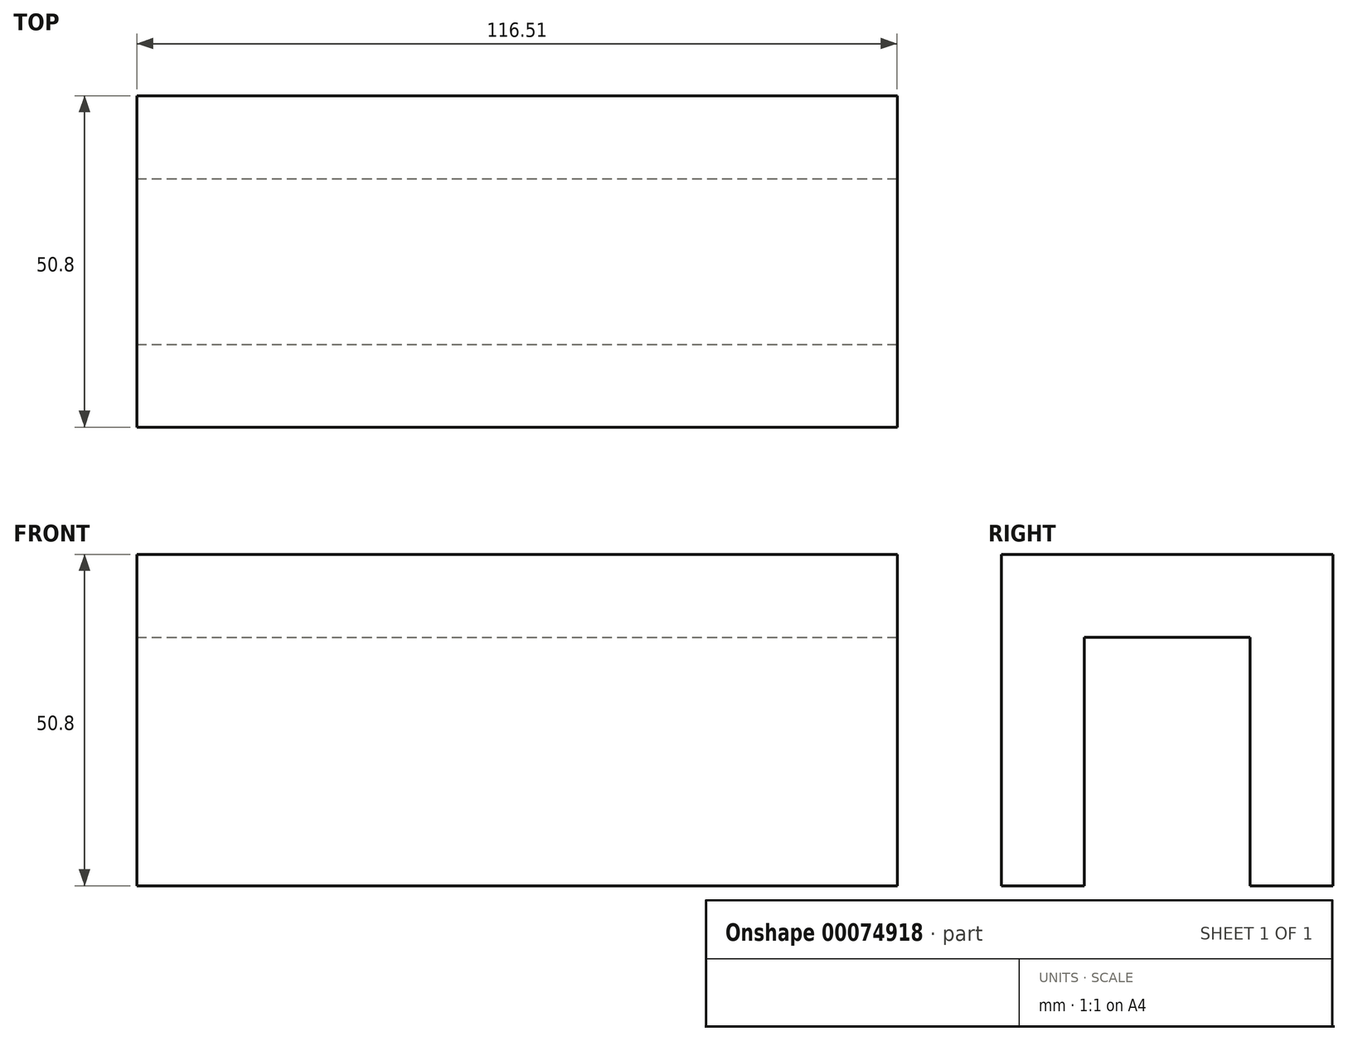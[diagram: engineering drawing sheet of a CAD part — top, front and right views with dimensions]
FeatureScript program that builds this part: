
annotation { "Feature Type Name" : "Feature", "Feature Type Description" : "" }
export const myFeature = defineFeature(function(context is Context, id is Id, definition is map)
    precondition{}
    {
        {
            var Q0;
            Q0=qCreatedBy(makeId("Top.planeOp"),FACE);
            var sketch = newSketch(context, id + "F0", { "sketchPlane" : qUnion([Q0])});
            skLineSegment(sketch, "E0", {"start": v(57.24, 0) * mm, "end": v(57.24, 50.8) * mm});
            skLineSegment(sketch, "E1", {"start": v(57.24, 50.8) * mm, "end": v(-59.27, 50.8) * mm});
            skLineSegment(sketch, "E2", {"start": v(-59.27, 50.8) * mm, "end": v(-59.27, 0) * mm});
            skLineSegment(sketch, "E3", {"start": v(-59.27, 0) * mm, "end": v(57.24, 0) * mm});
            skSolve(sketch);
        }
        {
            var Q0;
            Q0 = qSketchRegion(id + "F0", true);
            extrude(context, id + "F1", {"entities" : qUnion([Q0]), "depth" : 12.7 * mm});
        }
        {
            var Q0;
            Q0=makeQuery(id+"F1.opExtrude","CAP_FACE",FACE,{"disambiguationData":[OSD([sQuery(id+"F0.wireOp",EDGE,"E0"),sQuery(id+"F0.wireOp",EDGE,"E1"),sQuery(id+"F0.wireOp",EDGE,"E2"),sQuery(id+"F0.wireOp",EDGE,"E3")])],"isStart":true});
            var sketch = newSketch(context, id + "F2", { "sketchPlane" : qUnion([Q0])});
            skLineSegment(sketch, "E4", {"start": v(57.24, 0) * mm, "end": v(-59.27, 0) * mm});
            skLineSegment(sketch, "E5", {"start": v(-59.27, 0) * mm, "end": v(-59.27, -12.7) * mm});
            skLineSegment(sketch, "E6", {"start": v(-59.27, -12.7) * mm, "end": v(57.24, -12.7) * mm});
            skLineSegment(sketch, "E7", {"start": v(57.24, -12.7) * mm, "end": v(57.24, 0) * mm});
            skSolve(sketch);
        }
        {
            var Q0;
            Q0 = qSketchRegion(id + "F2", true);
            extrude(context, id + "F3", {"entities" : qUnion([Q0]), "operationType" : NewBodyOperationType.ADD, "depth" : 38.1 * mm});
        }
        {
            var Q0;
            Q0=makeQuery(id+"F1.opExtrude","CAP_FACE",FACE,{"disambiguationData":[OSD([sQuery(id+"F0.wireOp",EDGE,"E0"),sQuery(id+"F0.wireOp",EDGE,"E1"),sQuery(id+"F0.wireOp",EDGE,"E2"),sQuery(id+"F0.wireOp",EDGE,"E3")])],"isStart":true});
            var sketch = newSketch(context, id + "F4", { "sketchPlane" : qUnion([Q0])});
            skLineSegment(sketch, "E8", {"start": v(-59.27, -50.8) * mm, "end": v(-59.27, -38.1) * mm});
            skLineSegment(sketch, "E9", {"start": v(-59.27, -38.1) * mm, "end": v(57.24, -38.1) * mm});
            skLineSegment(sketch, "E10", {"start": v(57.24, -38.1) * mm, "end": v(57.24, -50.8) * mm});
            skLineSegment(sketch, "E11", {"start": v(57.24, -50.8) * mm, "end": v(-59.27, -50.8) * mm});
            skSolve(sketch);
        }
        {
            var Q0;
            Q0 = qSketchRegion(id + "F4", true);
            extrude(context, id + "F5", {"entities" : qUnion([Q0]), "operationType" : NewBodyOperationType.ADD, "depth" : 38.1 * mm});
        }
    });
